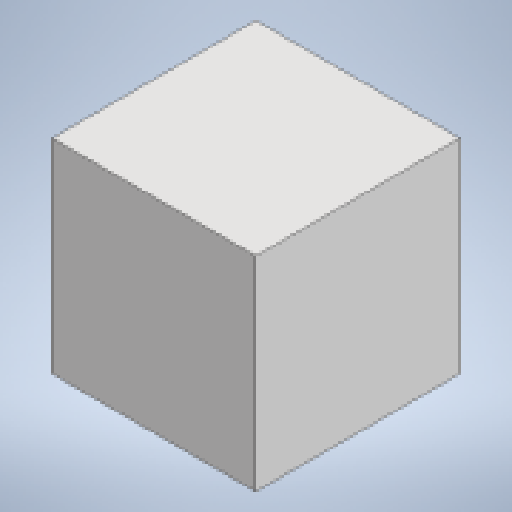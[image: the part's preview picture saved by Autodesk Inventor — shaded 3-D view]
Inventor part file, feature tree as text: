
AUTODESK INVENTOR PART (.ipt)
format: ipt  version: 2025 (Build 290162010, 162A)  size: 108,544 bytes
history: native  units: mm
features: extrude x1, sketch x1
ambient origin geometry x8: Origin, YZ Plane, XZ Plane, XY Plane, X Axis, Y Axis, Z Axis, Center Point
bodies: Volumenkörper1 (feature_tree)
feature tree (2):
  extrude  "Extrusion1"  Depth=32.0mm
  sketch  "Skizze1"  dims[d0=32.0mm d1=32.0mm d2=32.0mm d3=0.0mm]
